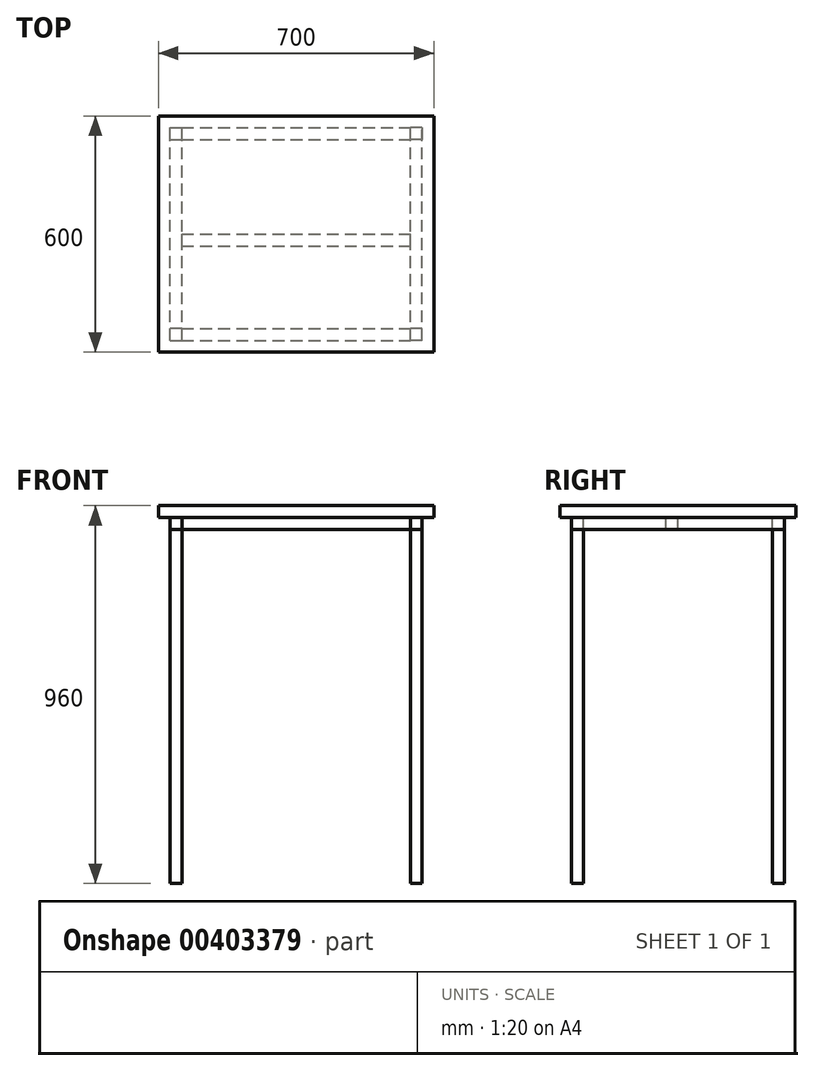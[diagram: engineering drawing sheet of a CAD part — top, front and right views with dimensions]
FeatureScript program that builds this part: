
annotation { "Feature Type Name" : "Feature", "Feature Type Description" : "" }
export const myFeature = defineFeature(function(context is Context, id is Id, definition is map)
    precondition{}
    {
        {
            var Q0;
            Q0=qCreatedBy(makeId("Top.planeOp"),FACE);
            var sketch = newSketch(context, id + "F0", { "sketchPlane" : qUnion([Q0])});
            skLineSegment(sketch, "E0.bottom", {"start": v(350, 300) * mm, "end": v(-350, 300) * mm});
            skLineSegment(sketch, "E0.top", {"start": v(350, -300) * mm, "end": v(-350, -300) * mm});
            skLineSegment(sketch, "E0.left", {"start": v(350, 300) * mm, "end": v(350, -300) * mm});
            skLineSegment(sketch, "E0.right", {"start": v(-350, 300) * mm, "end": v(-350, -300) * mm});
            skPoint(sketch, "E0.middle", {"position": v(0, 0) * mm});
            skSolve(sketch);
        }
        {
            var Q0;
            Q0 = qSketchRegion(id + "F0", true);
            extrude(context, id + "F1", {"entities" : qUnion([Q0]), "depth" : 30 * mm});
        }
        {
            var Q0;
            Q0=makeQuery(id+"F1.opExtrude","CAP_FACE",FACE,{"disambiguationData":[OSD([sQuery(id+"F0.wireOp",EDGE,"E0.bottom"),sQuery(id+"F0.wireOp",EDGE,"E0.top"),sQuery(id+"F0.wireOp",EDGE,"E0.left"),sQuery(id+"F0.wireOp",EDGE,"E0.right")])],"isStart":true});
            var sketch = newSketch(context, id + "F2", { "sketchPlane" : qUnion([Q0])});
            skLineSegment(sketch, "E1.bottom", {"start": v(320, 270) * mm, "end": v(290, 270) * mm});
            skLineSegment(sketch, "E1.top", {"start": v(320, -270) * mm, "end": v(290, -270) * mm});
            skLineSegment(sketch, "E1.left", {"start": v(320, 270) * mm, "end": v(320, -270) * mm});
            skLineSegment(sketch, "E1.right", {"start": v(290, 270) * mm, "end": v(290, -270) * mm});
            skLineSegment(sketch, "E2.MirrorCS", {"start": v(-290, 270) * mm, "end": v(-290, -270) * mm});
            skLineSegment(sketch, "E3.MirrorCS", {"start": v(-320, 270) * mm, "end": v(-320, -270) * mm});
            skLineSegment(sketch, "E4.MirrorCS", {"start": v(-320, 270) * mm, "end": v(-290, 270) * mm});
            skLineSegment(sketch, "E5.MirrorCS", {"start": v(-320, -270) * mm, "end": v(-290, -270) * mm});
            skLineSegment(sketch, "E6.bottom", {"start": v(-290, 270) * mm, "end": v(290, 270) * mm});
            skLineSegment(sketch, "E6.top", {"start": v(-290, 240) * mm, "end": v(290, 240) * mm});
            skLineSegment(sketch, "E6.left", {"start": v(-290, 270) * mm, "end": v(-290, 240) * mm});
            skLineSegment(sketch, "E6.right", {"start": v(290, 270) * mm, "end": v(290, 240) * mm});
            skLineSegment(sketch, "E7.bottom", {"start": v(-290, -270) * mm, "end": v(290, -270) * mm});
            skLineSegment(sketch, "E7.top", {"start": v(-290, -240) * mm, "end": v(290, -240) * mm});
            skLineSegment(sketch, "E7.left", {"start": v(-290, -270) * mm, "end": v(-290, -240) * mm});
            skLineSegment(sketch, "E7.right", {"start": v(290, -270) * mm, "end": v(290, -240) * mm});
            skLineSegment(sketch, "E8.0.1.0", {"start": v(-290, 30) * mm, "end": v(290, 30) * mm});
            skLineSegment(sketch, "E8.0.1.1", {"start": v(-290, 0) * mm, "end": v(290, 0) * mm});
            skLineSegment(sketch, "E8.direction1", {"start": v(-290, 240) * mm, "end": v(-265, 240) * mm, "construction": true});
            skLineSegment(sketch, "E8.direction2", {"start": v(-290, 240) * mm, "end": v(-290, 0) * mm, "construction": true});
            skSolve(sketch);
        }
        {
            var Q0;
            Q0=makeQuery(id+"F2.imprint","IMPRINT",FACE,{"disambiguationData":[TD([[makeQuery(id+"F2.imprint","IMPRINT",EDGE,{"derivedFrom":sQuery(id+"F2.wireOp",EDGE,"E6.bottom")}),-1.0]])]});
            var Q1;
            Q1=makeQuery(id+"F2.imprint","IMPRINT",FACE,{"disambiguationData":[TD([[makeQuery(id+"F2.imprint","IMPRINT",EDGE,{"derivedFrom":sQuery(id+"F2.wireOp",EDGE,"E7.bottom")}),1.0]])]});
            extrude(context, id + "F3", {"entities" : qUnion([Q0, Q1]), "depth" : 30 * mm});
        }
        {
            var Q0;
            Q0=makeQuery(id+"F2.imprint","IMPRINT",FACE,{"disambiguationData":[TD([[makeQuery(id+"F2.imprint","IMPRINT",EDGE,{"derivedFrom":sQuery(id+"F2.wireOp",EDGE,"E2.MirrorCS")}),-1.0]])]});
            var Q1;
            Q1=makeQuery(id+"F2.imprint","IMPRINT",FACE,{"disambiguationData":[TD([[makeQuery(id+"F2.imprint","IMPRINT",EDGE,{"derivedFrom":sQuery(id+"F2.wireOp",EDGE,"E1.top")}),-1.0]])]});
            extrude(context, id + "F4", {"entities" : qUnion([Q0, Q1]), "depth" : 30 * mm});
        }
        {
            var Q0;
            {var subQ0=sQuery(id+"F2.wireOp",EDGE,"E8.0.1.0");Q0=makeQuery(id+"F2.imprint","IMPRINT",FACE,{"disambiguationData":[TD([[makeQuery(id+"F2.imprint","IMPRINT",EDGE,{"derivedFrom":subQ0}),-1.0]])]});}
            extrude(context, id + "F5", {"entities" : qUnion([Q0]), "depth" : 30 * mm});
        }
        {
            var Q0;
            Q0=makeQuery(id+"F4.opExtrude","CAP_FACE",FACE,{"disambiguationData":[OSD([sQuery(id+"F2.wireOp",EDGE,"E2.MirrorCS"),sQuery(id+"F2.wireOp",EDGE,"E3.MirrorCS"),sQuery(id+"F2.wireOp",EDGE,"E4.MirrorCS"),sQuery(id+"F2.wireOp",EDGE,"E5.MirrorCS"),sQuery(id+"F2.wireOp",EDGE,"E6.left"),sQuery(id+"F2.wireOp",EDGE,"E7.left")])],"isStart":false});
            var sketch = newSketch(context, id + "F6", { "sketchPlane" : qUnion([Q0])});
            skLineSegment(sketch, "E9.bottom", {"start": v(-290, 270) * mm, "end": v(-320, 270) * mm});
            skLineSegment(sketch, "E9.top", {"start": v(-290, 240) * mm, "end": v(-320, 240) * mm});
            skLineSegment(sketch, "E9.left", {"start": v(-290, 270) * mm, "end": v(-290, 240) * mm});
            skLineSegment(sketch, "E9.right", {"start": v(-320, 270) * mm, "end": v(-320, 240) * mm});
            skPoint(sketch, "E10.0", {"position": v(320, 270) * mm});
            skPoint(sketch, "E10.1", {"position": v(320, -270) * mm});
            skPoint(sketch, "E10.2", {"position": v(-320, -270) * mm});
            skLineSegment(sketch, "E11.bottom", {"start": v(320, 270) * mm, "end": v(290, 270) * mm});
            skLineSegment(sketch, "E11.top", {"start": v(320, 240) * mm, "end": v(290, 240) * mm});
            skLineSegment(sketch, "E11.left", {"start": v(320, 270) * mm, "end": v(320, 240) * mm});
            skLineSegment(sketch, "E11.right", {"start": v(290, 270) * mm, "end": v(290, 240) * mm});
            skLineSegment(sketch, "E12.bottom", {"start": v(320, -270) * mm, "end": v(290, -270) * mm});
            skLineSegment(sketch, "E12.top", {"start": v(320, -240) * mm, "end": v(290, -240) * mm});
            skLineSegment(sketch, "E12.left", {"start": v(320, -270) * mm, "end": v(320, -240) * mm});
            skLineSegment(sketch, "E12.right", {"start": v(290, -270) * mm, "end": v(290, -240) * mm});
            skLineSegment(sketch, "E13.bottom", {"start": v(-320, -270) * mm, "end": v(-290, -270) * mm});
            skLineSegment(sketch, "E13.top", {"start": v(-320, -240) * mm, "end": v(-290, -240) * mm});
            skLineSegment(sketch, "E13.left", {"start": v(-320, -270) * mm, "end": v(-320, -240) * mm});
            skLineSegment(sketch, "E13.right", {"start": v(-290, -270) * mm, "end": v(-290, -240) * mm});
            skSolve(sketch);
        }
        {
            var Q0;
            Q0=makeQuery(id+"F6.imprint","IMPRINT",FACE,{"disambiguationData":[TD([[makeQuery(id+"F6.imprint","IMPRINT",EDGE,{"derivedFrom":sQuery(id+"F6.wireOp",EDGE,"E9.bottom")}),-1.0]])]});
            var Q1;
            Q1=makeQuery(id+"F6.imprint","IMPRINT",FACE,{"disambiguationData":[TD([[makeQuery(id+"F6.imprint","IMPRINT",EDGE,{"derivedFrom":sQuery(id+"F6.wireOp",EDGE,"E13.bottom")}),1.0]])]});
            var Q2;
            Q2=makeQuery(id+"F6.imprint","IMPRINT",FACE,{"disambiguationData":[TD([[makeQuery(id+"F6.imprint","IMPRINT",EDGE,{"derivedFrom":sQuery(id+"F6.wireOp",EDGE,"E12.bottom")}),-1.0]])]});
            var Q3;
            Q3=makeQuery(id+"F6.imprint","IMPRINT",FACE,{"disambiguationData":[TD([[makeQuery(id+"F6.imprint","IMPRINT",EDGE,{"derivedFrom":sQuery(id+"F6.wireOp",EDGE,"E11.bottom")}),1.0]])]});
            extrude(context, id + "F7", {"entities" : qUnion([Q0, Q1, Q2, Q3]), "depth" : 900 * mm});
        }
    });
